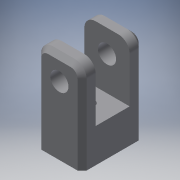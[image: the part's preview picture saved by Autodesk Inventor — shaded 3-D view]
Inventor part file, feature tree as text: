
AUTODESK INVENTOR PART (.ipt)
format: ipt  version: 2017 (Build 210142000, 142)  size: 156,160 bytes
history: native  units: mm
features: extrude x4, sketch x3, chamfer x2, fillet x1
ambient origin geometry x8: Origin, YZ Plane, XZ Plane, XY Plane, X Axis, Y Axis, Z Axis, Center Point
bodies: Solid1 (feature_tree)
feature tree (10):
  sketch  "Sketch1"  dims[d0=15.0mm d1=20.0mm]
  extrude  "Extrusion1"  Depth=20.0mm
  extrude  "Extrusion2"  Depth=15.0mm TaperAngle=0.0deg
  extrude  "Extrusion3"  Depth=4.0mm
  fillet  "Fillet1"  Radius=10.0mm
  extrude  "Extrusion4"  Depth=25.0mm TaperAngle=0.0deg
  chamfer  "Chamfer1"  Distance=5.0mm
  chamfer  "Chamfer2"  Distance=4.3mm
  sketch  "Sketch2"  dims[d2=6.0mm d3=15.0mm d4=0.0mm]
  sketch  "Sketch3"  dims[d5=25.0mm d6=0.0mm d7=8.0mm d8=10.0mm d9=25.0mm d10=0.0mm d11=5.0mm d12=4.3mm d13=25.0mm d14=0.0mm d15=2.0mm d16=2.0mm d17=45.0deg d18=4.0mm d19=2.0mm d20=45.0deg]
